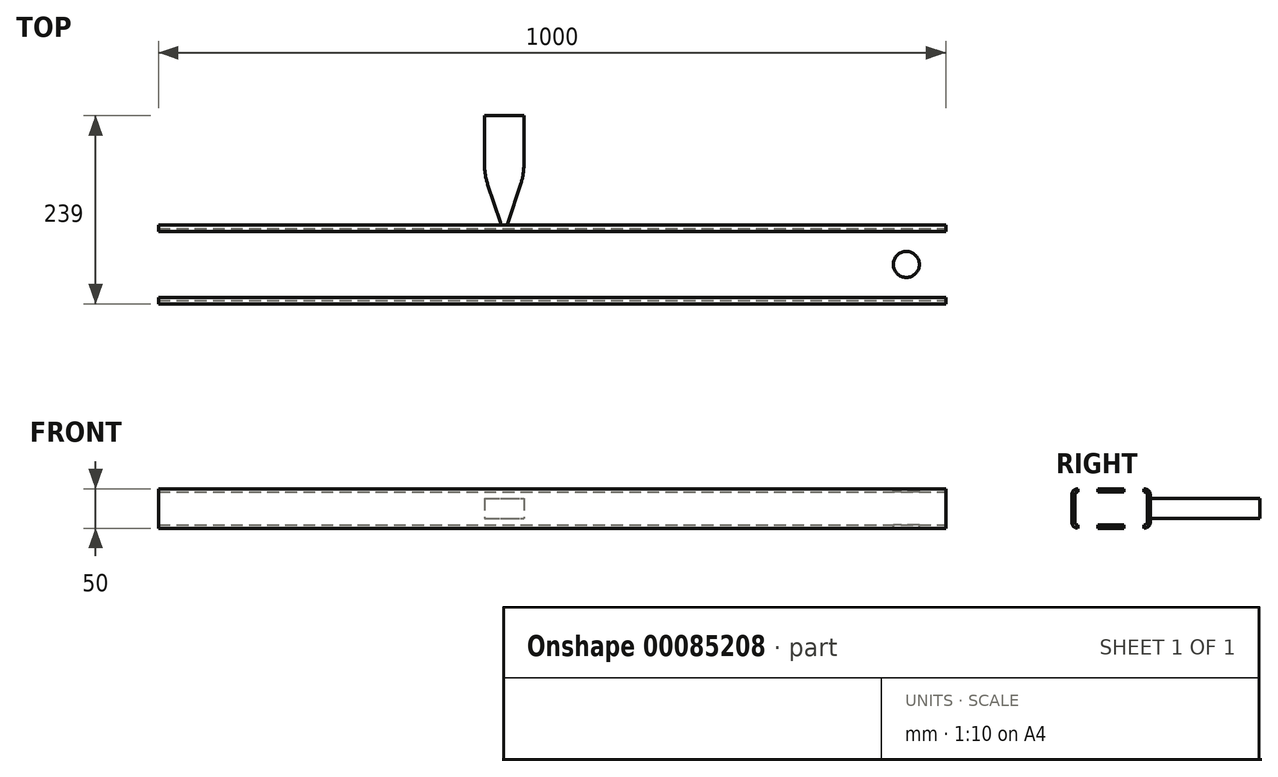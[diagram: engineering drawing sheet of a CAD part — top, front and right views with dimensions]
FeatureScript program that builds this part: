
annotation { "Feature Type Name" : "Feature", "Feature Type Description" : "" }
export const myFeature = defineFeature(function(context is Context, id is Id, definition is map)
    precondition{}
    {
        {
            var Q0;
            Q0=qCreatedBy(makeId("Right.planeOp"),FACE);
            var sketch = newSketch(context, id + "F0", { "sketchPlane" : qUnion([Q0])});
            skLineSegment(sketch, "E0.bottom", {"start": v(-50, 25) * mm, "end": v(50, 25) * mm});
            skLineSegment(sketch, "E0.top", {"start": v(-50, -25) * mm, "end": v(50, -25) * mm});
            skLineSegment(sketch, "E0.left", {"start": v(-50, 25) * mm, "end": v(-50, -25) * mm});
            skLineSegment(sketch, "E0.right", {"start": v(50, 25) * mm, "end": v(50, -25) * mm});
            skSolve(sketch);
        }
        {
            var Q0;
            Q0=makeQuery(id+"F0.imprint","IMPRINT",FACE,{"disambiguationData":[TD([[makeQuery(id+"F0.imprint","IMPRINT",EDGE,{"derivedFrom":sQuery(id+"F0.wireOp",EDGE,"E0.bottom")}),-1.0]])]});
            extrude(context, id + "F1", {"entities" : qUnion([Q0]), "depth" : 1000 * mm});
        }
        {
            var Q0;
            Q0=makeQuery(id+"F1.opExtrude","SWEPT_EDGE",EDGE,{"disambiguationData":[OSD([sQuery(id+"F0.wireOp",EDGE,"E0.bottom"),sQuery(id+"F0.wireOp",EDGE,"E0.left")])]});
            var Q1;
            Q1=makeQuery(id+"F1.opExtrude","SWEPT_EDGE",EDGE,{"disambiguationData":[OSD([sQuery(id+"F0.wireOp",EDGE,"E0.top"),sQuery(id+"F0.wireOp",EDGE,"E0.left")])]});
            var Q2;
            Q2=makeQuery(id+"F1.opExtrude","SWEPT_EDGE",EDGE,{"disambiguationData":[OSD([sQuery(id+"F0.wireOp",EDGE,"E0.bottom"),sQuery(id+"F0.wireOp",EDGE,"E0.right")])]});
            var Q3;
            Q3=makeQuery(id+"F1.opExtrude","SWEPT_EDGE",EDGE,{"disambiguationData":[OSD([sQuery(id+"F0.wireOp",EDGE,"E0.top"),sQuery(id+"F0.wireOp",EDGE,"E0.right")])]});
            fillet(context, id + "F2", {"entities" : qUnion([Q0, Q1, Q2, Q3]), "radius" : 8 * mm, "tangentPropagation" : true, "allowEdgeOverflow" : false});
        }
        {
            var Q0;
            Q0=makeQuery(id+"F1.opExtrude","CAP_FACE",FACE,{"disambiguationData":[OSD([sQuery(id+"F0.wireOp",EDGE,"E0.bottom"),sQuery(id+"F0.wireOp",EDGE,"E0.top"),sQuery(id+"F0.wireOp",EDGE,"E0.left"),sQuery(id+"F0.wireOp",EDGE,"E0.right")])],"isStart":false});
            var Q1;
            Q1=makeQuery(id+"F1.opExtrude","CAP_FACE",FACE,{"disambiguationData":[OSD([sQuery(id+"F0.wireOp",EDGE,"E0.bottom"),sQuery(id+"F0.wireOp",EDGE,"E0.top"),sQuery(id+"F0.wireOp",EDGE,"E0.left"),sQuery(id+"F0.wireOp",EDGE,"E0.right")])],"isStart":true});
            shell(context, id + "F3", {"entities" : qUnion([Q0, Q1]), "thickness" : 4 * mm});
        }
        {
            var Q0;
            Q0=makeQuery(id+"F1.opExtrude","SWEPT_FACE",FACE,{"disambiguationData":[OSD([sQuery(id+"F0.wireOp",EDGE,"E0.bottom")])]});
            var sketch = newSketch(context, id + "F4", { "sketchPlane" : qUnion([Q0])});
            skLineSegment(sketch, "E1", {"start": v(500, -285.52) * mm, "end": v(500, 337.9) * mm, "construction": true});
            skCircle(sketch, "E2", {"center": v(50, 0) * mm, "radius": 16.5 * mm});
            skCircle(sketch, "E3.MirrorC", {"center": v(950, 0) * mm, "radius": 16.5 * mm});
            skSolve(sketch);
        }
        {
            var Q0;
            Q0=makeQuery(id+"F4.imprint","IMPRINT",FACE,{"disambiguationData":[TD([[makeQuery(id+"F4.imprint","IMPRINT",EDGE,{"derivedFrom":sQuery(id+"F4.wireOp",EDGE,"E2")}),1.0]])]});
            var Q1;
            Q1=makeQuery(id+"F4.imprint","IMPRINT",FACE,{"disambiguationData":[TD([[makeQuery(id+"F4.imprint","IMPRINT",EDGE,{"derivedFrom":sQuery(id+"F4.wireOp",EDGE,"E3.MirrorC")}),-1.0]])]});
            extrude(context, id + "F5", {"entities" : qUnion([Q0, Q1]), "operationType" : NewBodyOperationType.REMOVE, "endBound" : BoundingType.THROUGH_ALL, "oppositeDirection" : true, "depth" : 25 * mm});
        }
        {
            var Q0;
            Q0=qCreatedBy(makeId("Top.planeOp"),FACE);
            var sketch = newSketch(context, id + "F6", { "sketchPlane" : qUnion([Q0])});
            skLineSegment(sketch, "E4.top", {"start": v(414.08, 200) * mm, "end": v(464.08, 200) * mm});
            skLineSegment(sketch, "E4.left", {"start": v(414.08, 125) * mm, "end": v(414.08, 200) * mm});
            skLineSegment(sketch, "E4.right", {"start": v(464.08, 125) * mm, "end": v(464.08, 200) * mm});
            skLineSegment(sketch, "E5", {"start": v(414.08, 125) * mm, "end": v(434.34, 64.23) * mm});
            skLineSegment(sketch, "E6", {"start": v(443.83, 64.23) * mm, "end": v(464.08, 125) * mm});
            skPoint(sketch, "E7.orphan", {"position": v(464.08, 50) * mm});
            skPoint(sketch, "E4.bottom.start.orphan", {"position": v(414.08, 50) * mm});
            skPoint(sketch, "E8.visualSharp", {"position": v(439.08, 50) * mm});
            skArc(sketch, "E8.filletArc", {"start": v(434.34, 64.23) * mm, "mid": v(439.08, 60.81) * mm, "end": v(443.83, 64.23) * mm});
            skLineSegment(sketch, "E9", {"start": v(439.08, 60.81) * mm, "end": v(460.43, 60.81) * mm, "construction": true});
            skSolve(sketch);
        }
        {
            var Q0;
            Q0=makeQuery(id+"F6.imprint","IMPRINT",FACE,{"disambiguationData":[TD([[makeQuery(id+"F6.imprint","IMPRINT",EDGE,{"derivedFrom":sQuery(id+"F6.wireOp",EDGE,"E4.top")}),-1.0]])]});
            extrude(context, id + "F7", {"entities" : qUnion([Q0]), "endBound" : BoundingType.SYMMETRIC, "depth" : 25 * mm});
        }
        {
            var Q0;
            Q0=makeQuery(id+"F7.opExtrude","SWEPT_EDGE",EDGE,{"disambiguationData":[OSD([sQuery(id+"F6.wireOp",EDGE,"E4.left"),sQuery(id+"F6.wireOp",EDGE,"E5")])]});
            var Q1;
            Q1=makeQuery(id+"F7.opExtrude","SWEPT_EDGE",EDGE,{"disambiguationData":[OSD([sQuery(id+"F6.wireOp",EDGE,"E4.right"),sQuery(id+"F6.wireOp",EDGE,"E6")])]});
            fillet(context, id + "F8", {"entities" : qUnion([Q0, Q1]), "radius" : 80 * mm, "tangentPropagation" : true, "allowEdgeOverflow" : false});
        }
        {
            var Q0;
            Q0=makeQuery(id+"F7.opExtrude","SWEPT_BODY",BODY,{"disambiguationData":[OSD([sQuery(id+"F6.wireOp",EDGE,"E4.top"),sQuery(id+"F6.wireOp",EDGE,"E4.left"),sQuery(id+"F6.wireOp",EDGE,"E4.right"),sQuery(id+"F6.wireOp",EDGE,"E5"),sQuery(id+"F6.wireOp",EDGE,"E6"),sQuery(id+"F6.wireOp",EDGE,"E8.filletArc")])]});
            transform(context, id + "F9", {"entities" : qUnion([Q0]), "transformType" : TransformType.TRANSLATION_3D, "dx" : 0 * mm, "dy" : -11 * mm, "dz" : 0 * mm, "makeCopy" : false});
        }
    });
